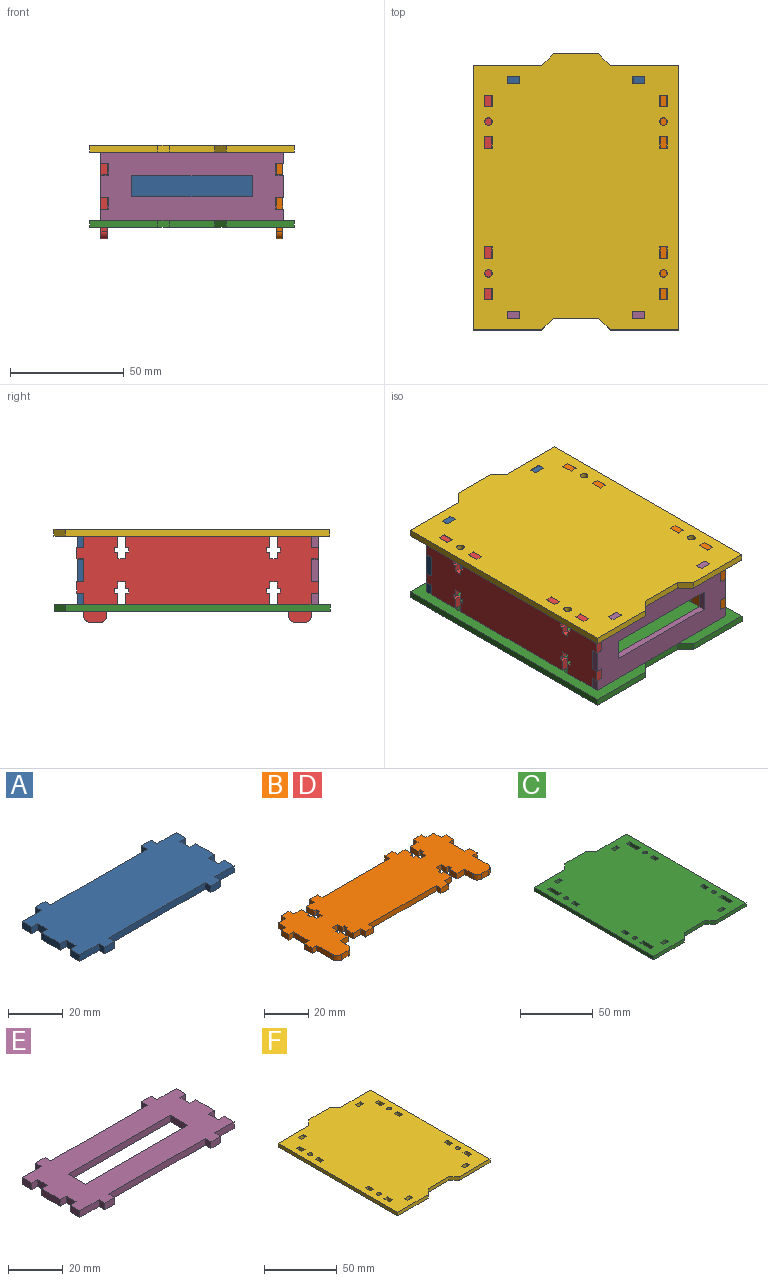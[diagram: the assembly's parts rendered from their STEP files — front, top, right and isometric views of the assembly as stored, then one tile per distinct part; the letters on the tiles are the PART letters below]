
ASSEMBLY  parts=6 mates=5
PART A: 38 faces, bbox 80x36x3 mm
  f0: plane 3x3mm, normal (1,0,0), area 9mm2, adj f1,f35,f36,f37
  f1: plane 5x3mm, normal (0,1,0), area 15mm2, adj f0,f2,f36,f37
  f2: plane 3x3mm, normal (-1,0,0), area 9mm2, adj f1,f3,f36,f37
  f3: plane 50x3mm, normal (0,1,0), area 150mm2, adj f2,f4,f36,f37
  f4: plane 3x3mm, normal (1,0,0), area 9mm2, adj f3,f5,f36,f37
  f5: plane 5x3mm, normal (0,1,0), area 15mm2, adj f4,f6,f36,f37
  f6: plane 3x3mm, normal (-1,0,0), area 9mm2, adj f5,f7,f36,f37
  f7: plane 10x3mm, normal (0,1,0), area 30mm2, adj f6,f8,f36,f37
  f8: plane 5x3mm, normal (-1,0,0), area 15mm2, adj f7,f9,f36,f37
  f9: plane 3.1x3mm, normal (0,-1,0), area 9.3mm2, adj f8,f10,f36,f37
  f10: plane 5.1x3mm, normal (-1,0,0), area 15.3mm2, adj f9,f11,f36,f37
  f11: plane 3.1x3mm, normal (0,1,0), area 9.3mm2, adj f10,f12,f36,f37
  f12: plane 9.8x3mm, normal (-1,0,0), area 29.4mm2, adj f11,f13,f36,f37
  f13: plane 3.1x3mm, normal (0,-1,0), area 9.3mm2, adj f12,f14,f36,f37
  f14: plane 5.1x3mm, normal (-1,0,0), area 15.3mm2, adj f13,f15,f36,f37
  f15: plane 3.1x3mm, normal (0,1,0), area 9.3mm2, adj f14,f16,f36,f37
  f16: plane 5x3mm, normal (-1,0,0), area 15mm2, adj f15,f17,f36,f37
  f17: plane 10x3mm, normal (0,-1,0), area 30mm2, adj f16,f18,f36,f37
  f18: plane 3x3mm, normal (-1,0,0), area 9mm2, adj f17,f19,f36,f37
  f19: plane 5x3mm, normal (0,-1,0), area 15mm2, adj f18,f20,f36,f37
  f20: plane 3x3mm, normal (1,0,0), area 9mm2, adj f19,f21,f36,f37
  f21: plane 50x3mm, normal (0,-1,0), area 150mm2, adj f20,f22,f36,f37
  f22: plane 3x3mm, normal (-1,0,0), area 9mm2, adj f21,f23,f36,f37
  f23: plane 5x3mm, normal (0,-1,0), area 15mm2, adj f22,f24,f36,f37
  f24: plane 3x3mm, normal (1,0,0), area 9mm2, adj f23,f25,f36,f37
  f25: plane 10x3mm, normal (0,-1,0), area 30mm2, adj f24,f26,f36,f37
  f26: plane 5x3mm, normal (1,0,0), area 15mm2, adj f25,f27,f36,f37
  f27: plane 3.1x3mm, normal (0,1,0), area 9.3mm2, adj f26,f28,f36,f37
  f28: plane 5.1x3mm, normal (1,0,0), area 15.3mm2, adj f27,f29,f36,f37
  f29: plane 3.1x3mm, normal (0,-1,0), area 9.3mm2, adj f28,f30,f36,f37
  f30: plane 9.8x3mm, normal (1,0,0), area 29.4mm2, adj f29,f31,f36,f37
  f31: plane 3.1x3mm, normal (0,1,0), area 9.3mm2, adj f30,f32,f36,f37
  f32: plane 5.1x3mm, normal (1,0,0), area 15.3mm2, adj f31,f33,f36,f37
  f33: plane 3.1x3mm, normal (0,-1,0), area 9.3mm2, adj f32,f34,f36,f37
  f34: plane 5x3mm, normal (1,0,0), area 15mm2, adj f33,f35,f36,f37
  f35: plane 10x3mm, normal (0,1,0), area 30mm2, adj f0,f34,f36,f37
  f36: plane 80x36mm, normal (0,0,1), area 2396.8mm2, adj f0,f1,f2,f3,f4,f5,f6,f7
  f37: plane 80x36mm, normal (0,0,-1), area 2396.8mm2, adj f0,f1,f2,f3,f4,f5,f6,f7
PART B: 102 faces, bbox 106x41x3 mm
  f0: plane 5x3mm, normal (0,-1,0), area 15mm2, adj f1,f99,f100,f101
  f1: plane 3x3mm, normal (1,0,0), area 9mm2, adj f0,f2,f100,f101
  f2: plane 43.4x3mm, normal (0,-1,0), area 130.2mm2, adj f1,f3,f100,f101
  f3: plane 3x3mm, normal (-1,0,0), area 9mm2, adj f2,f4,f100,f101
  f4: plane 5x3mm, normal (0,-1,0), area 15mm2, adj f3,f5,f100,f101
  f5: plane 3x3mm, normal (1,0,0), area 9mm2, adj f4,f6,f100,f101
  f6: plane 5x3mm, normal (0,-1,0), area 15mm2, adj f5,f7,f100,f101
  f7: plane 5x3mm, normal (1,0,0), area 15mm2, adj f6,f8,f100,f101
  f8: plane 3x1.35mm, normal (0,1,0), area 4mm2, adj f7,f9,f100,f101
  f9: plane 3x2mm, normal (1,0,0), area 6mm2, adj f8,f10,f100,f101
  f10: plane 3x1.35mm, normal (0,-1,0), area 4mm2, adj f9,f11,f100,f101
  f11: plane 3x3mm, normal (1,0,0), area 9mm2, adj f10,f12,f100,f101
  f12: plane 3.3x3mm, normal (0,-1,0), area 9.9mm2, adj f11,f13,f100,f101
  f13: plane 3x3mm, normal (-1,0,0), area 9mm2, adj f12,f14,f100,f101
  f14: plane 3x1.35mm, normal (0,-1,0), area 4mm2, adj f13,f15,f100,f101
  f15: plane 3x2mm, normal (-1,0,0), area 6mm2, adj f14,f16,f100,f101
  f16: plane 3x1.35mm, normal (0,1,0), area 4mm2, adj f15,f17,f100,f101
  f17: plane 5x3mm, normal (-1,0,0), area 15mm2, adj f16,f18,f100,f101
  f18: plane 5x3mm, normal (0,-1,0), area 15mm2, adj f17,f19,f100,f101
  f19: plane 5x3mm, normal (-1,0,0), area 15mm2, adj f18,f20,f100,f101
  f20: cylinder r=3mm len=3mm, axis (0,0,-1), area 14.1mm2, adj f19,f21,f100,f101
  f21: plane 4x3mm, normal (0,-1,0), area 12mm2, adj f20,f22,f100,f101
  f22: cylinder r=3mm len=3mm, axis (0,0,-1), area 14.1mm2, adj f21,f23,f100,f101
  f23: plane 10x3mm, normal (1,0,0), area 30mm2, adj f22,f24,f100,f101
  f24: plane 3x3mm, normal (0,-1,0), area 9mm2, adj f23,f25,f100,f101
  f25: plane 5x3mm, normal (1,0,0), area 15mm2, adj f24,f26,f100,f101
  f26: plane 3x3mm, normal (0,1,0), area 9mm2, adj f25,f27,f100,f101
  f27: plane 10x3mm, normal (1,0,0), area 30mm2, adj f26,f28,f100,f101
  f28: plane 3x3mm, normal (0,-1,0), area 9mm2, adj f27,f29,f100,f101
  f29: plane 5x3mm, normal (1,0,0), area 15mm2, adj f28,f30,f100,f101
  f30: plane 3x3mm, normal (0,1,0), area 9mm2, adj f29,f31,f100,f101
  f31: plane 5x3mm, normal (1,0,0), area 15mm2, adj f30,f32,f100,f101
  f32: plane 5x3mm, normal (0,1,0), area 15mm2, adj f31,f33,f100,f101
  f33: plane 3x3mm, normal (1,0,0), area 9mm2, adj f32,f34,f100,f101
  f34: plane 5x3mm, normal (0,1,0), area 15mm2, adj f33,f35,f100,f101
  f35: plane 3x3mm, normal (-1,0,0), area 9mm2, adj f34,f36,f100,f101
  f36: plane 5x3mm, normal (0,1,0), area 15mm2, adj f35,f37,f100,f101
  f37: plane 5x3mm, normal (-1,0,0), area 15mm2, adj f36,f38,f100,f101
  f38: plane 3x1.35mm, normal (0,-1,0), area 4mm2, adj f37,f39,f100,f101
  f39: plane 3x2mm, normal (-1,0,0), area 6mm2, adj f38,f40,f100,f101
  f40: plane 3x1.35mm, normal (0,1,0), area 4mm2, adj f39,f41,f100,f101
  f41: plane 3x3mm, normal (-1,0,0), area 9mm2, adj f40,f42,f100,f101
  f42: plane 3.3x3mm, normal (0,1,0), area 9.9mm2, adj f41,f43,f100,f101
  f43: plane 3x3mm, normal (1,0,0), area 9mm2, adj f42,f44,f100,f101
  f44: plane 3x1.35mm, normal (0,1,0), area 4mm2, adj f43,f45,f100,f101
  f45: plane 3x2mm, normal (1,0,0), area 6mm2, adj f44,f46,f100,f101
  f46: plane 3x1.35mm, normal (0,-1,0), area 4mm2, adj f45,f47,f100,f101
  f47: plane 5x3mm, normal (1,0,0), area 15mm2, adj f46,f48,f100,f101
  f48: plane 5x3mm, normal (0,1,0), area 15mm2, adj f47,f49,f100,f101
  f49: plane 3x3mm, normal (1,0,0), area 9mm2, adj f48,f50,f100,f101
  f50: plane 5x3mm, normal (0,1,0), area 15mm2, adj f49,f51,f100,f101
  f51: plane 3x3mm, normal (-1,0,0), area 9mm2, adj f50,f52,f100,f101
  f52: plane 43.4x3mm, normal (0,1,0), area 130.2mm2, adj f51,f53,f100,f101
  f53: plane 3x3mm, normal (1,0,0), area 9mm2, adj f52,f54,f100,f101
  f54: plane 5x3mm, normal (0,1,0), area 15mm2, adj f53,f55,f100,f101
  f55: plane 3x3mm, normal (-1,0,0), area 9mm2, adj f54,f56,f100,f101
  f56: plane 5x3mm, normal (0,1,0), area 15mm2, adj f55,f57,f100,f101
  f57: plane 5x3mm, normal (-1,0,0), area 15mm2, adj f56,f58,f100,f101
  f58: plane 3x1.35mm, normal (0,-1,0), area 4.1mm2, adj f57,f59,f100,f101
  f59: plane 3x2mm, normal (-1,0,0), area 6mm2, adj f58,f60,f100,f101
  f60: plane 3x1.35mm, normal (0,1,0), area 4.1mm2, adj f59,f61,f100,f101
  f61: plane 3x3mm, normal (-1,0,0), area 9mm2, adj f60,f62,f100,f101
  f62: plane 3.3x3mm, normal (0,1,0), area 9.9mm2, adj f61,f63,f100,f101
  f63: plane 3x3mm, normal (1,0,0), area 9mm2, adj f62,f64,f100,f101
  f64: plane 3x1.35mm, normal (0,1,0), area 4mm2, adj f63,f65,f100,f101
  f65: plane 3x2mm, normal (1,0,0), area 6mm2, adj f64,f66,f100,f101
  f66: plane 3x1.35mm, normal (0,-1,0), area 4mm2, adj f65,f67,f100,f101
  f67: plane 5x3mm, normal (1,0,0), area 15mm2, adj f66,f68,f100,f101
  f68: plane 5x3mm, normal (0,1,0), area 15mm2, adj f67,f69,f100,f101
  f69: plane 3x3mm, normal (1,0,0), area 9mm2, adj f68,f70,f100,f101
  f70: plane 5x3mm, normal (0,1,0), area 15mm2, adj f69,f71,f100,f101
  f71: plane 3x3mm, normal (-1,0,0), area 9mm2, adj f70,f72,f100,f101
  f72: plane 5x3mm, normal (0,1,0), area 15mm2, adj f71,f73,f100,f101
  f73: plane 5x3mm, normal (-1,0,0), area 15mm2, adj f72,f74,f100,f101
  f74: plane 3x3mm, normal (0,1,0), area 9mm2, adj f73,f75,f100,f101
  f75: plane 5x3mm, normal (-1,0,0), area 15mm2, adj f74,f76,f100,f101
  f76: plane 3x3mm, normal (0,-1,0), area 9mm2, adj f75,f77,f100,f101
  f77: plane 10x3mm, normal (-1,0,0), area 30mm2, adj f76,f78,f100,f101
  f78: plane 3x3mm, normal (0,1,0), area 9mm2, adj f77,f79,f100,f101
  f79: plane 5x3mm, normal (-1,0,0), area 15mm2, adj f78,f80,f100,f101
  f80: plane 3x3mm, normal (0,-1,0), area 9mm2, adj f79,f81,f100,f101
  f81: plane 10x3mm, normal (-1,0,0), area 30mm2, adj f80,f82,f100,f101
  f82: cylinder r=3mm len=3mm, axis (0,0,-1), area 14.1mm2, adj f81,f83,f100,f101
  f83: plane 4x3mm, normal (0,-1,0), area 12mm2, adj f82,f84,f100,f101
  f84: cylinder r=3mm len=3mm, axis (0,0,-1), area 14.1mm2, adj f83,f85,f100,f101
  f85: plane 5x3mm, normal (1,0,0), area 15mm2, adj f84,f86,f100,f101
  f86: plane 5x3mm, normal (0,-1,0), area 15mm2, adj f85,f87,f100,f101
  f87: plane 5x3mm, normal (1,0,0), area 15mm2, adj f86,f88,f100,f101
  f88: plane 3x1.35mm, normal (0,1,0), area 4mm2, adj f87,f89,f100,f101
  f89: plane 3x2mm, normal (1,0,0), area 6mm2, adj f88,f90,f100,f101
  f90: plane 3x1.35mm, normal (0,-1,0), area 4mm2, adj f89,f91,f100,f101
  f91: plane 3x3mm, normal (1,0,0), area 9mm2, adj f90,f92,f100,f101
  f92: plane 3.3x3mm, normal (0,-1,0), area 9.9mm2, adj f91,f93,f100,f101
  f93: plane 3x3mm, normal (-1,0,0), area 9mm2, adj f92,f94,f100,f101
  f94: plane 3x1.35mm, normal (0,-1,0), area 4.1mm2, adj f93,f95,f100,f101
  f95: plane 3x2mm, normal (-1,0,0), area 6mm2, adj f94,f96,f100,f101
  f96: plane 3x1.35mm, normal (0,1,0), area 4.1mm2, adj f95,f97,f100,f101
  f97: plane 5x3mm, normal (-1,0,0), area 15mm2, adj f96,f98,f100,f101
  f98: plane 5x3mm, normal (0,-1,0), area 15mm2, adj f97,f99,f100,f101
  f99: plane 3x3mm, normal (-1,0,0), area 9mm2, adj f0,f98,f100,f101
  f100: plane 106x41mm, normal (0,0,1), area 3148.7mm2, adj f0,f1,f2,f3,f4,f5,f6,f7
  f101: plane 106x41mm, normal (0,0,-1), area 3148.7mm2, adj f0,f1,f2,f3,f4,f5,f6,f7
PART C: 66 faces, bbox 90x121.2x3 mm
  f0: plane 3.1x3mm, normal (-1,0,0), area 9.3mm2, adj f1,f63,f64,f65
  f1: plane 5.1x3mm, normal (0,1,0), area 15.3mm2, adj f0,f2,f64,f65
  f2: plane 3.1x3mm, normal (1,0,0), area 9.3mm2, adj f1,f63,f64,f65
  f3: plane 3.1x3mm, normal (0,1,0), area 9.3mm2, adj f4,f47,f64,f65
  f4: plane 5.1x3mm, normal (1,0,0), area 15.3mm2, adj f3,f5,f64,f65
  f5: plane 3.1x3mm, normal (0,-1,0), area 9.3mm2, adj f4,f47,f64,f65
  f6: plane 3.1x3mm, normal (0,-1,0), area 9.3mm2, adj f7,f48,f64,f65
  f7: plane 10.1x3mm, normal (-1,0,0), area 30.3mm2, adj f6,f8,f64,f65
  f8: plane 3.1x3mm, normal (0,1,0), area 9.3mm2, adj f7,f48,f64,f65
  f9: plane 5.1x3mm, normal (0,1,0), area 15.3mm2, adj f10,f49,f64,f65
  f10: plane 3.1x3mm, normal (1,0,0), area 9.3mm2, adj f9,f11,f64,f65
  f11: plane 5.1x3mm, normal (0,-1,0), area 15.3mm2, adj f10,f49,f64,f65
  f12: plane 5.1x3mm, normal (1,0,0), area 15.3mm2, adj f13,f50,f64,f65
  f13: plane 3.1x3mm, normal (0,-1,0), area 9.3mm2, adj f12,f14,f64,f65
  f14: plane 5.1x3mm, normal (-1,0,0), area 15.3mm2, adj f13,f50,f64,f65
  f15: plane 3.1x3mm, normal (0,-1,0), area 9.3mm2, adj f16,f51,f64,f65
  f16: plane 5.1x3mm, normal (-1,0,0), area 15.3mm2, adj f15,f17,f64,f65
  f17: plane 3.1x3mm, normal (0,1,0), area 9.3mm2, adj f16,f51,f64,f65
  f18: plane 3.1x3mm, normal (0,1,0), area 9.3mm2, adj f19,f52,f64,f65
  f19: plane 10.1x3mm, normal (1,0,0), area 30.3mm2, adj f18,f20,f64,f65
  f20: plane 3.1x3mm, normal (0,-1,0), area 9.3mm2, adj f19,f52,f64,f65
  f21: plane 3.1x3mm, normal (0,1,0), area 9.3mm2, adj f22,f53,f64,f65
  f22: plane 10.1x3mm, normal (1,0,0), area 30.3mm2, adj f21,f23,f64,f65
  f23: plane 3.1x3mm, normal (0,-1,0), area 9.3mm2, adj f22,f53,f64,f65
  f24: plane 5x5mm, normal (0.71,-0.71,0), area 21.2mm2, adj f25,f54,f64,f65
  f25: plane 20x3mm, normal (0,-1,0), area 60mm2, adj f24,f26,f64,f65
  f26: plane 5x5mm, normal (-0.71,-0.71,0), area 21.2mm2, adj f25,f27,f64,f65
  f27: plane 30x3mm, normal (0,-1,0), area 90mm2, adj f26,f28,f64,f65
  f28: plane 116.2x3mm, normal (1,0,0), area 348.6mm2, adj f27,f29,f64,f65
  f29: plane 30x3mm, normal (0,1,0), area 90mm2, adj f28,f30,f64,f65
  f30: plane 5x5mm, normal (0.71,0.71,0), area 21.2mm2, adj f29,f31,f64,f65
  f31: plane 20x3mm, normal (0,1,0), area 60mm2, adj f30,f32,f64,f65
  f32: plane 5x5mm, normal (-0.71,0.71,0), area 21.2mm2, adj f31,f33,f64,f65
  f33: plane 30x3mm, normal (0,1,0), area 90mm2, adj f32,f34,f64,f65
  f34: plane 116.2x3mm, normal (-1,0,0), area 348.6mm2, adj f33,f54,f64,f65
  f35: plane 3.1x3mm, normal (-1,0,0), area 9.3mm2, adj f36,f59,f64,f65
  f36: plane 5.1x3mm, normal (0,1,0), area 15.3mm2, adj f35,f37,f64,f65
  f37: plane 3.1x3mm, normal (1,0,0), area 9.3mm2, adj f36,f59,f64,f65
  f38: plane 3.1x3mm, normal (0,-1,0), area 9.3mm2, adj f39,f60,f64,f65
  f39: plane 5.1x3mm, normal (-1,0,0), area 15.3mm2, adj f38,f40,f64,f65
  f40: plane 3.1x3mm, normal (0,1,0), area 9.3mm2, adj f39,f60,f64,f65
  f41: plane 10.1x3mm, normal (1,0,0), area 30.3mm2, adj f42,f61,f64,f65
  f42: plane 3.1x3mm, normal (0,-1,0), area 9.3mm2, adj f41,f43,f64,f65
  f43: plane 10.1x3mm, normal (-1,0,0), area 30.3mm2, adj f42,f61,f64,f65
  f44: plane 3.1x3mm, normal (-1,0,0), area 9.3mm2, adj f45,f62,f64,f65
  f45: plane 5.1x3mm, normal (0,1,0), area 15.3mm2, adj f44,f46,f64,f65
  f46: plane 3.1x3mm, normal (1,0,0), area 9.3mm2, adj f45,f62,f64,f65
  f47: plane 5.1x3mm, normal (-1,0,0), area 15.3mm2, adj f3,f5,f64,f65
  f48: plane 10.1x3mm, normal (1,0,0), area 30.3mm2, adj f6,f8,f64,f65
  f49: plane 3.1x3mm, normal (-1,0,0), area 9.3mm2, adj f9,f11,f64,f65
  f50: plane 3.1x3mm, normal (0,1,0), area 9.3mm2, adj f12,f14,f64,f65
  f51: plane 5.1x3mm, normal (1,0,0), area 15.3mm2, adj f15,f17,f64,f65
  f52: plane 10.1x3mm, normal (-1,0,0), area 30.3mm2, adj f18,f20,f64,f65
  f53: plane 10.1x3mm, normal (-1,0,0), area 30.3mm2, adj f21,f23,f64,f65
  f54: plane 30x3mm, normal (0,-1,0), area 90mm2, adj f24,f34,f64,f65
  f55: cylinder r=1.65mm len=3.3mm, axis (0,0,-1), area 31.1mm2, adj f64,f65
  f56: cylinder r=1.65mm len=3.3mm, axis (0,0,-1), area 31.1mm2, adj f64,f65
  f57: cylinder r=1.65mm len=3.3mm, axis (0,0,-1), area 31.1mm2, adj f64,f65
  f58: cylinder r=1.65mm len=3.3mm, axis (0,0,-1), area 31.1mm2, adj f64,f65
  f59: plane 5.1x3mm, normal (0,-1,0), area 15.3mm2, adj f35,f37,f64,f65
  f60: plane 5.1x3mm, normal (1,0,0), area 15.3mm2, adj f38,f40,f64,f65
  f61: plane 3.1x3mm, normal (0,1,0), area 9.3mm2, adj f41,f43,f64,f65
  f62: plane 5.1x3mm, normal (0,-1,0), area 15.3mm2, adj f44,f46,f64,f65
  f63: plane 5.1x3mm, normal (0,-1,0), area 15.3mm2, adj f0,f2,f64,f65
  f64: plane 121.2x90mm, normal (0,0,1), area 10172.1mm2, adj f0,f1,f2,f3,f4,f5,f6,f7
  f65: plane 121.2x90mm, normal (0,0,-1), area 10172.1mm2, adj f0,f1,f2,f3,f4,f5,f6,f7
PART D: same geometry as B
PART E: 42 faces, bbox 80x36x3 mm
  f0: plane 53x3mm, normal (0,-1,0), area 159mm2, adj f1,f39,f40,f41
  f1: plane 9.25x3mm, normal (-1,0,0), area 27.7mm2, adj f0,f2,f40,f41
  f2: plane 53x3mm, normal (0,1,0), area 159mm2, adj f1,f39,f40,f41
  f3: plane 9.8x3mm, normal (1,0,0), area 29.4mm2, adj f4,f38,f40,f41
  f4: plane 3.1x3mm, normal (0,1,0), area 9.3mm2, adj f3,f5,f40,f41
  f5: plane 5.1x3mm, normal (1,0,0), area 15.3mm2, adj f4,f6,f40,f41
  f6: plane 3.1x3mm, normal (0,-1,0), area 9.3mm2, adj f5,f7,f40,f41
  f7: plane 5x3mm, normal (1,0,0), area 15mm2, adj f6,f8,f40,f41
  f8: plane 10x3mm, normal (0,1,0), area 30mm2, adj f7,f9,f40,f41
  f9: plane 3x3mm, normal (1,0,0), area 9mm2, adj f8,f10,f40,f41
  f10: plane 5x3mm, normal (0,1,0), area 15mm2, adj f9,f11,f40,f41
  f11: plane 3x3mm, normal (-1,0,0), area 9mm2, adj f10,f12,f40,f41
  f12: plane 50x3mm, normal (0,1,0), area 150mm2, adj f11,f13,f40,f41
  f13: plane 3x3mm, normal (1,0,0), area 9mm2, adj f12,f14,f40,f41
  f14: plane 5x3mm, normal (0,1,0), area 15mm2, adj f13,f15,f40,f41
  f15: plane 3x3mm, normal (-1,0,0), area 9mm2, adj f14,f16,f40,f41
  f16: plane 10x3mm, normal (0,1,0), area 30mm2, adj f15,f17,f40,f41
  f17: plane 5x3mm, normal (-1,0,0), area 15mm2, adj f16,f18,f40,f41
  f18: plane 3.1x3mm, normal (0,-1,0), area 9.3mm2, adj f17,f19,f40,f41
  f19: plane 5.1x3mm, normal (-1,0,0), area 15.3mm2, adj f18,f20,f40,f41
  f20: plane 3.1x3mm, normal (0,1,0), area 9.3mm2, adj f19,f21,f40,f41
  f21: plane 9.8x3mm, normal (-1,0,0), area 29.4mm2, adj f20,f22,f40,f41
  f22: plane 3.1x3mm, normal (0,-1,0), area 9.3mm2, adj f21,f23,f40,f41
  f23: plane 5.1x3mm, normal (-1,0,0), area 15.3mm2, adj f22,f24,f40,f41
  f24: plane 3.1x3mm, normal (0,1,0), area 9.3mm2, adj f23,f25,f40,f41
  f25: plane 5x3mm, normal (-1,0,0), area 15mm2, adj f24,f26,f40,f41
  f26: plane 10x3mm, normal (0,-1,0), area 30mm2, adj f25,f27,f40,f41
  f27: plane 3x3mm, normal (-1,0,0), area 9mm2, adj f26,f28,f40,f41
  f28: plane 5x3mm, normal (0,-1,0), area 15mm2, adj f27,f29,f40,f41
  f29: plane 3x3mm, normal (1,0,0), area 9mm2, adj f28,f30,f40,f41
  f30: plane 50x3mm, normal (0,-1,0), area 150mm2, adj f29,f31,f40,f41
  f31: plane 3x3mm, normal (-1,0,0), area 9mm2, adj f30,f32,f40,f41
  f32: plane 5x3mm, normal (0,-1,0), area 15mm2, adj f31,f33,f40,f41
  f33: plane 3x3mm, normal (1,0,0), area 9mm2, adj f32,f34,f40,f41
  f34: plane 10x3mm, normal (0,-1,0), area 30mm2, adj f33,f35,f40,f41
  f35: plane 5x3mm, normal (1,0,0), area 15mm2, adj f34,f36,f40,f41
  f36: plane 3.1x3mm, normal (0,1,0), area 9.3mm2, adj f35,f37,f40,f41
  f37: plane 5.1x3mm, normal (1,0,0), area 15.3mm2, adj f36,f38,f40,f41
  f38: plane 3.1x3mm, normal (0,-1,0), area 9.3mm2, adj f3,f37,f40,f41
  f39: plane 9.25x3mm, normal (1,0,0), area 27.8mm2, adj f0,f2,f40,f41
  f40: plane 80x36mm, normal (0,0,1), area 1906.5mm2, adj f0,f1,f2,f3,f4,f5,f6,f7
  f41: plane 80x36mm, normal (0,0,-1), area 1906.5mm2, adj f0,f1,f2,f3,f4,f5,f6,f7
PART F: 66 faces, bbox 90x121.2x3 mm
  f0: plane 3.1x3mm, normal (0,1,0), area 9.3mm2, adj f1,f63,f64,f65
  f1: plane 5.1x3mm, normal (1,0,0), area 15.3mm2, adj f0,f2,f64,f65
  f2: plane 3.1x3mm, normal (0,-1,0), area 9.3mm2, adj f1,f63,f64,f65
  f3: plane 5x5mm, normal (-0.71,0.71,0), area 21.2mm2, adj f4,f47,f64,f65
  f4: plane 30x3mm, normal (0,1,0), area 90mm2, adj f3,f5,f64,f65
  f5: plane 116.2x3mm, normal (-1,0,0), area 348.6mm2, adj f4,f6,f64,f65
  f6: plane 30x3mm, normal (0,-1,0), area 90mm2, adj f5,f7,f64,f65
  f7: plane 5x5mm, normal (0.71,-0.71,0), area 21.2mm2, adj f6,f8,f64,f65
  f8: plane 20x3mm, normal (0,-1,0), area 60mm2, adj f7,f9,f64,f65
  f9: plane 5x5mm, normal (-0.71,-0.71,0), area 21.2mm2, adj f8,f10,f64,f65
  f10: plane 30x3mm, normal (0,-1,0), area 90mm2, adj f9,f11,f64,f65
  f11: plane 116.2x3mm, normal (1,0,0), area 348.6mm2, adj f10,f12,f64,f65
  f12: plane 30x3mm, normal (0,1,0), area 90mm2, adj f11,f13,f64,f65
  f13: plane 5x5mm, normal (0.71,0.71,0), area 21.2mm2, adj f12,f47,f64,f65
  f14: plane 3.1x3mm, normal (0,-1,0), area 9.3mm2, adj f15,f48,f64,f65
  f15: plane 5.1x3mm, normal (-1,0,0), area 15.3mm2, adj f14,f16,f64,f65
  f16: plane 3.1x3mm, normal (0,1,0), area 9.3mm2, adj f15,f48,f64,f65
  f17: plane 3.1x3mm, normal (0,-1,0), area 9.3mm2, adj f18,f49,f64,f65
  f18: plane 5.1x3mm, normal (-1,0,0), area 15.3mm2, adj f17,f19,f64,f65
  f19: plane 3.1x3mm, normal (0,1,0), area 9.3mm2, adj f18,f49,f64,f65
  f20: plane 3.1x3mm, normal (-1,0,0), area 9.3mm2, adj f21,f50,f64,f65
  f21: plane 5.1x3mm, normal (0,1,0), area 15.3mm2, adj f20,f22,f64,f65
  f22: plane 3.1x3mm, normal (1,0,0), area 9.3mm2, adj f21,f50,f64,f65
  f23: plane 5.1x3mm, normal (0,-1,0), area 15.3mm2, adj f24,f51,f64,f65
  f24: plane 3.1x3mm, normal (-1,0,0), area 9.3mm2, adj f23,f25,f64,f65
  f25: plane 5.1x3mm, normal (0,1,0), area 15.3mm2, adj f24,f51,f64,f65
  f26: plane 3.1x3mm, normal (0,-1,0), area 9.3mm2, adj f27,f52,f64,f65
  f27: plane 5.1x3mm, normal (-1,0,0), area 15.3mm2, adj f26,f28,f64,f65
  f28: plane 3.1x3mm, normal (0,1,0), area 9.3mm2, adj f27,f52,f64,f65
  f29: plane 3.1x3mm, normal (0,1,0), area 9.3mm2, adj f30,f53,f64,f65
  f30: plane 5.1x3mm, normal (1,0,0), area 15.3mm2, adj f29,f31,f64,f65
  f31: plane 3.1x3mm, normal (0,-1,0), area 9.3mm2, adj f30,f53,f64,f65
  f32: plane 5.1x3mm, normal (-1,0,0), area 15.3mm2, adj f33,f58,f64,f65
  f33: plane 3.1x3mm, normal (0,1,0), area 9.3mm2, adj f32,f34,f64,f65
  f34: plane 5.1x3mm, normal (1,0,0), area 15.3mm2, adj f33,f58,f64,f65
  f35: plane 5.1x3mm, normal (1,0,0), area 15.3mm2, adj f36,f59,f64,f65
  f36: plane 3.1x3mm, normal (0,-1,0), area 9.3mm2, adj f35,f37,f64,f65
  f37: plane 5.1x3mm, normal (-1,0,0), area 15.3mm2, adj f36,f59,f64,f65
  f38: plane 5.1x3mm, normal (0,1,0), area 15.3mm2, adj f39,f60,f64,f65
  f39: plane 3.1x3mm, normal (1,0,0), area 9.3mm2, adj f38,f40,f64,f65
  f40: plane 5.1x3mm, normal (0,-1,0), area 15.3mm2, adj f39,f60,f64,f65
  f41: plane 3.1x3mm, normal (1,0,0), area 9.3mm2, adj f42,f61,f64,f65
  f42: plane 5.1x3mm, normal (0,-1,0), area 15.3mm2, adj f41,f43,f64,f65
  f43: plane 3.1x3mm, normal (-1,0,0), area 9.3mm2, adj f42,f61,f64,f65
  f44: plane 3.1x3mm, normal (0,1,0), area 9.3mm2, adj f45,f62,f64,f65
  f45: plane 5.1x3mm, normal (1,0,0), area 15.3mm2, adj f44,f46,f64,f65
  f46: plane 3.1x3mm, normal (0,-1,0), area 9.3mm2, adj f45,f62,f64,f65
  f47: plane 20x3mm, normal (0,1,0), area 60mm2, adj f3,f13,f64,f65
  f48: plane 5.1x3mm, normal (1,0,0), area 15.3mm2, adj f14,f16,f64,f65
  f49: plane 5.1x3mm, normal (1,0,0), area 15.3mm2, adj f17,f19,f64,f65
  f50: plane 5.1x3mm, normal (0,-1,0), area 15.3mm2, adj f20,f22,f64,f65
  f51: plane 3.1x3mm, normal (1,0,0), area 9.3mm2, adj f23,f25,f64,f65
  f52: plane 5.1x3mm, normal (1,0,0), area 15.3mm2, adj f26,f28,f64,f65
  f53: plane 5.1x3mm, normal (-1,0,0), area 15.3mm2, adj f29,f31,f64,f65
  f54: cylinder r=1.65mm len=3.3mm, axis (0,0,-1), area 31.1mm2, adj f64,f65
  f55: cylinder r=1.65mm len=3.3mm, axis (0,0,-1), area 31.1mm2, adj f64,f65
  f56: cylinder r=1.65mm len=3.3mm, axis (0,0,-1), area 31.1mm2, adj f64,f65
  f57: cylinder r=1.65mm len=3.3mm, axis (0,0,-1), area 31.1mm2, adj f64,f65
  f58: plane 3.1x3mm, normal (0,-1,0), area 9.3mm2, adj f32,f34,f64,f65
  f59: plane 3.1x3mm, normal (0,1,0), area 9.3mm2, adj f35,f37,f64,f65
  f60: plane 3.1x3mm, normal (-1,0,0), area 9.3mm2, adj f38,f40,f64,f65
  f61: plane 5.1x3mm, normal (0,1,0), area 15.3mm2, adj f41,f43,f64,f65
  f62: plane 5.1x3mm, normal (-1,0,0), area 15.3mm2, adj f44,f46,f64,f65
  f63: plane 5.1x3mm, normal (-1,0,0), area 15.3mm2, adj f0,f2,f64,f65
  f64: plane 121.2x90mm, normal (0,0,1), area 10234.1mm2, adj f0,f1,f2,f3,f4,f5,f6,f7
  f65: plane 121.2x90mm, normal (0,0,-1), area 10234.1mm2, adj f0,f1,f2,f3,f4,f5,f6,f7
PLACE A rot(axis=(-1,0,0),90deg) t=(-4.9,108.15,33)mm
PLACE B rot(axis=(0.58,0.58,0.58),120deg) t=(-8.05,8.2,3)mm
PLACE C t=(-5,0,0)mm
PLACE D rot(axis=(0.58,-0.58,-0.58),120deg) t=(-82,108.2,3)mm
PLACE E rot(axis=(0,-0.71,-0.71),180deg) t=(-85,5.1,3)mm
PLACE F t=(-5,0.1,33)mm
MATE fastened D.f100 <-> C.f48  axis (-1,0,0) through (-85,18.2,3)mm
MATE fastened A.f3 <-> C.f64  axis (0,0,-1) through (-69.9,109.65,3)mm
MATE fastened E.f40 <-> C.f62  axis (0,1,0) through (-75,8.1,3)mm
MATE fastened F.f65 <-> D.f32  axis (0,0,-1) through (-85,13.2,33)mm
MATE fastened B.f86 <-> C.f64  axis (0,0,-1) through (-6.55,18.2,3)mm
